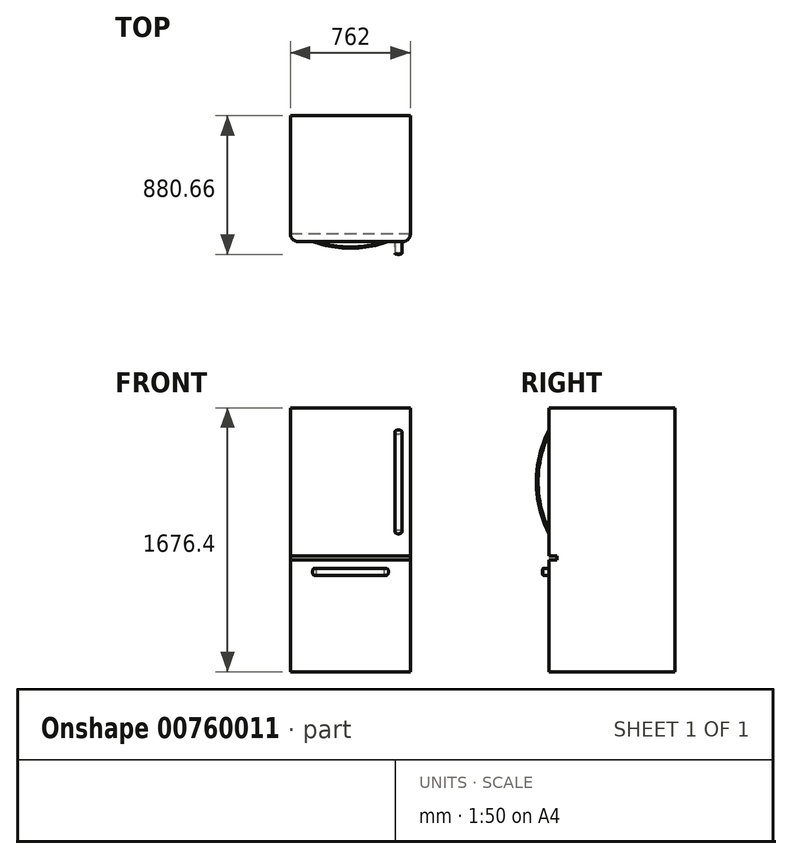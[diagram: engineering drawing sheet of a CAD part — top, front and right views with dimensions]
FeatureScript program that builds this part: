
annotation { "Feature Type Name" : "Feature", "Feature Type Description" : "" }
export const myFeature = defineFeature(function(context is Context, id is Id, definition is map)
    precondition{}
    {
        {
            var Q0;
            Q0=qCreatedBy(makeId("Top.planeOp"),FACE);
            var sketch = newSketch(context, id + "F0", { "sketchPlane" : qUnion([Q0])});
            skLineSegment(sketch, "E0.bottom", {"start": v(381, -400.05) * mm, "end": v(-381, -400.05) * mm});
            skLineSegment(sketch, "E0.top", {"start": v(381, 400.05) * mm, "end": v(-381, 400.05) * mm});
            skLineSegment(sketch, "E0.left", {"start": v(381, -400.05) * mm, "end": v(381, 400.05) * mm});
            skLineSegment(sketch, "E0.right", {"start": v(-381, -400.05) * mm, "end": v(-381, 400.05) * mm});
            skPoint(sketch, "E0.middle", {"position": v(0, 0) * mm});
            skSolve(sketch);
        }
        {
            var Q0;
            Q0=makeQuery(id+"F0.imprint","IMPRINT",FACE,{"disambiguationData":[TD([[makeQuery(id+"F0.imprint","IMPRINT",EDGE,{"derivedFrom":sQuery(id+"F0.wireOp",EDGE,"E0.bottom")}),-1.0]])]});
            extrude(context, id + "F1", {"entities" : qUnion([Q0]), "depth" : 1676.4 * mm, "offsetDistance" : 25.4 * mm});
        }
        {
            var Q0;
            Q0=makeQuery(id+"F1.opExtrude","SWEPT_EDGE",EDGE,{"disambiguationData":[OSD([sQuery(id+"F0.wireOp",EDGE,"E0.bottom"),sQuery(id+"F0.wireOp",EDGE,"E0.left")])]});
            var Q1;
            Q1=makeQuery(id+"F1.opExtrude","SWEPT_EDGE",EDGE,{"disambiguationData":[OSD([sQuery(id+"F0.wireOp",EDGE,"E0.bottom"),sQuery(id+"F0.wireOp",EDGE,"E0.right")])]});
            fillet(context, id + "F2", {"entities" : qUnion([Q0, Q1]), "radius" : 50.8 * mm, "tangentPropagation" : true, "allowEdgeOverflow" : false});
        }
        {
            var Q0;
            Q0=makeQuery(id+"F1.opExtrude","SWEPT_FACE",FACE,{"disambiguationData":[OSD([sQuery(id+"F0.wireOp",EDGE,"E0.left")])]});
            var sketch = newSketch(context, id + "F3", { "sketchPlane" : qUnion([Q0])});
            skLineSegment(sketch, "E1.bottom", {"start": v(-407.2, 736.6) * mm, "end": v(-349.25, 736.6) * mm});
            skLineSegment(sketch, "E1.top", {"start": v(-407.2, 711.2) * mm, "end": v(-349.25, 711.2) * mm});
            skLineSegment(sketch, "E1.left", {"start": v(-407.2, 736.6) * mm, "end": v(-407.2, 711.2) * mm});
            skLineSegment(sketch, "E1.right", {"start": v(-349.25, 736.6) * mm, "end": v(-349.25, 711.2) * mm});
            skSolve(sketch);
        }
        {
            var Q0;
            Q0=makeQuery(id+"F3.imprint","IMPRINT",FACE,{"disambiguationData":[TD([[makeQuery(id+"F3.imprint","IMPRINT",EDGE,{"derivedFrom":sQuery(id+"F3.wireOp",EDGE,"E1.bottom")}),-1.0]])]});
            extrude(context, id + "F4", {"entities" : qUnion([Q0]), "operationType" : NewBodyOperationType.REMOVE, "endBound" : BoundingType.THROUGH_ALL, "oppositeDirection" : true, "depth" : 25.4 * mm, "offsetDistance" : 25.4 * mm});
        }
        {
            var Q0;
            Q0=makeQuery(id+"F1.opExtrude","SWEPT_FACE",FACE,{"disambiguationData":[OSD([sQuery(id+"F0.wireOp",EDGE,"E0.left")])]});
            cPlane(context, id + "F5", {"entities" : qUnion([Q0]), "cplaneType" : CPlaneType.OFFSET, "offset" : 76.2 * mm, "oppositeDirection" : true, "width" : 152.4 * mm, "height" : 152.4 * mm});
        }
        {
            var Q0;
            Q0=qCreatedBy(id+"F5.planeOp",FACE);
            var sketch = newSketch(context, id + "F6", { "sketchPlane" : qUnion([Q0])});
            skLineSegment(sketch, "E2.0", {"start": v(-400.05, 736.6) * mm, "end": v(-400.05, 1676.4) * mm});
            skArc(sketch, "E3", {"start": v(-400.05, 1524) * mm, "mid": v(-474.5, 1183.87) * mm, "end": v(-378.57, 849.17) * mm});
            skPoint(sketch, "E4.orphan", {"position": v(-400.05, 889) * mm});
            skSolve(sketch);
        }
        {
            var Q0;
            {var subQ2=sQuery(id+"F0.wireOp",EDGE,"E0.bottom");Q0=makeQuery(id+"F4.boolean.opBoolean","SPLIT",FACE,{"disambiguationData":[TD([makeQuery(id+"F4.opExtrude","SWEPT_FACE",FACE,{"disambiguationData":[OSD([sQuery(id+"F3.wireOp",EDGE,"E1.bottom")])]})])],"derivedFrom":makeQuery(id+"F1.opExtrude","SWEPT_FACE",FACE,{"disambiguationData":[OSD([subQ2])]})});}
            var sketch = newSketch(context, id + "F7", { "sketchPlane" : qUnion([Q0])});
            skPoint(sketch, "E5.0", {"position": v(304.8, 1524) * mm});
            skEllipse(sketch, "E6", {"center": v(304.8, 1524) * mm, "majorRadius": 22.23 * mm, "minorRadius": 12.7 * mm, "majorAxis": v(-1, 0)});
            skSolve(sketch);
        }
        {
            var Q0;
            {var subQ0=sQuery(id+"F7.wireOp",EDGE,"E6");var subQ1=sQuery(id+"F0.wireOp",EDGE,"E0.bottom");var subQ2=makeQuery(id+"F1.opExtrude","SWEPT_FACE",FACE,{"disambiguationData":[OSD([subQ1])]});var subQ3=sQuery(id+"F0.wireOp",EDGE,"E0.left");var subQ4=makeQuery(id+"F4.boolean.opBoolean","SPLIT",EDGE,{"disambiguationData":[TD([makeQuery(id+"F4.opExtrude","SWEPT_FACE",FACE,{"disambiguationData":[OSD([sQuery(id+"F3.wireOp",EDGE,"E1.bottom")])]})])],"derivedFrom":makeQuery(id+"F2.opFillet","BLEND_EDGE",EDGE,{"blendedFrom":[makeQuery(id+"F1.opExtrude","SWEPT_EDGE",EDGE,{"disambiguationData":[OSD([subQ1,subQ3])]}),subQ2],"blendedInto":[subQ2]})});var subQ5=makeQuery(id+"F7.imprint","INTERSECT",VERTEX,{"disambiguationData":[OD(0.0)],"derivedFrom":[subQ4,subQ0]});Q0=makeQuery(id+"F7.imprint","IMPRINT",FACE,{"disambiguationData":[TD([[makeQuery(id+"F7.imprint","IMPRINT",EDGE,{"disambiguationData":[TD([[subQ5,1.0]])],"derivedFrom":subQ0}),1.0]])]});}
            var Q1;
            {var subQ0=sQuery(id+"F7.wireOp",EDGE,"E6");var subQ1=sQuery(id+"F0.wireOp",EDGE,"E0.bottom");var subQ2=makeQuery(id+"F1.opExtrude","SWEPT_FACE",FACE,{"disambiguationData":[OSD([subQ1])]});var subQ3=sQuery(id+"F0.wireOp",EDGE,"E0.left");var subQ4=makeQuery(id+"F4.boolean.opBoolean","SPLIT",EDGE,{"disambiguationData":[TD([makeQuery(id+"F4.opExtrude","SWEPT_FACE",FACE,{"disambiguationData":[OSD([sQuery(id+"F3.wireOp",EDGE,"E1.bottom")])]})])],"derivedFrom":makeQuery(id+"F2.opFillet","BLEND_EDGE",EDGE,{"blendedFrom":[makeQuery(id+"F1.opExtrude","SWEPT_EDGE",EDGE,{"disambiguationData":[OSD([subQ1,subQ3])]}),subQ2],"blendedInto":[subQ2]})});var subQ5=makeQuery(id+"F7.imprint","INTERSECT",VERTEX,{"disambiguationData":[OD(0.0)],"derivedFrom":[subQ4,subQ0]});Q1=makeQuery(id+"F7.imprint","IMPRINT",FACE,{"disambiguationData":[TD([[makeQuery(id+"F7.imprint","IMPRINT",EDGE,{"disambiguationData":[TD([[subQ5,-1.0]])],"derivedFrom":subQ0}),1.0]])]});}
            var Q2;
            Q2=sQuery(id+"F6.wireOp",EDGE,"E3");
            sweep(context, id + "F8", {"operationType" : NewBodyOperationType.ADD, "profiles" : qUnion([Q0, Q1]), "path" : qUnion([Q2])});
        }
        {
            var Q0;
            Q0=makeQuery(id+"F4.boolean.opBoolean","COPY",FACE,{"derivedFrom":makeQuery(id+"F4.opExtrude","SWEPT_FACE",FACE,{"disambiguationData":[OSD([sQuery(id+"F3.wireOp",EDGE,"E1.top")])]})});
            cPlane(context, id + "F9", {"entities" : qUnion([Q0]), "cplaneType" : CPlaneType.OFFSET, "offset" : 76.2 * mm, "oppositeDirection" : true, "width" : 152.4 * mm, "height" : 152.4 * mm});
        }
        {
            var Q0;
            Q0=qCreatedBy(id+"F9.planeOp",FACE);
            var sketch = newSketch(context, id + "F10", { "sketchPlane" : qUnion([Q0])});
            skLineSegment(sketch, "E7.0", {"start": v(-330.2, -400.05) * mm, "end": v(330.2, -400.05) * mm});
            skArc(sketch, "E8", {"start": v(-228.6, -400.05) * mm, "mid": v(31.6, -437.09) * mm, "end": v(287.5, -377.1) * mm});
            skPoint(sketch, "E9.orphan", {"position": v(228.6, -400.05) * mm});
            skSolve(sketch);
        }
        {
            var Q0;
            {var subQ2=sQuery(id+"F0.wireOp",EDGE,"E0.bottom");Q0=makeQuery(id+"F4.boolean.opBoolean","SPLIT",FACE,{"disambiguationData":[TD([makeQuery(id+"F4.opExtrude","SWEPT_FACE",FACE,{"disambiguationData":[OSD([sQuery(id+"F3.wireOp",EDGE,"E1.top")])]})])],"derivedFrom":makeQuery(id+"F1.opExtrude","SWEPT_FACE",FACE,{"disambiguationData":[OSD([subQ2])]})});}
            var sketch = newSketch(context, id + "F11", { "sketchPlane" : qUnion([Q0])});
            skPoint(sketch, "E10.0", {"position": v(-228.6, 635) * mm});
            skEllipse(sketch, "E11", {"center": v(-228.6, 635) * mm, "majorRadius": 22.23 * mm, "minorRadius": 12.7 * mm, "majorAxis": v(0, -1)});
            skSolve(sketch);
        }
        {
            var Q0;
            Q0=makeQuery(id+"F11.imprint","IMPRINT",FACE,{"disambiguationData":[TD([[makeQuery(id+"F11.imprint","IMPRINT",EDGE,{"derivedFrom":sQuery(id+"F11.wireOp",EDGE,"E11")}),1.0]])]});
            var Q1;
            Q1=sQuery(id+"F10.wireOp",EDGE,"E8");
            sweep(context, id + "F12", {"operationType" : NewBodyOperationType.ADD, "profiles" : qUnion([Q0]), "path" : qUnion([Q1])});
        }
    });
